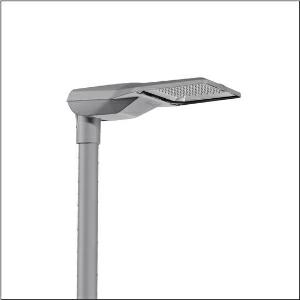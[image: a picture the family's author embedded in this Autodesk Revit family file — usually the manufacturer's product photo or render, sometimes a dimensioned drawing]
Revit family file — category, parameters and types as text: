
# Revit family: streetlight_sl_21_iq_midi___stw1_0a_5xe3e41g08mb_cdbd
name_source: partatom
category: Lighting Fixtures
units: mm (PartAtom-declared; Revit-internal decimal feet)

## family parameters
Cut with Voids When Loaded = No
Host = Face
Light Source = No
Part Type = Normal
Room Calculation Point = No
Round Connector Dimension = Use Diameter
Shared = No

## types (1)
- --- (1 x LED, 20360 lm, 146.7 W, 4000K)
    Apparent Load = 147 VA
    CIE Flux Codes = 38 75 98 100 100
    Color Rendering = 70
    Color Temperature = 4000K
    Default Elevation = 1800 mm
    Description = Streetlight SL 21 iQ midi, mast luminaire, primary light control with lens, of PMMA, primary optical cover: cover, of toughened safety glass, transparent, light distribution: STW1.0a, light emission: direct distribution, primary light characteristic: asymmetric, installation type: post-top, side-entry, LED, High Power LED, rated luminous flux: 20.360lm, luminous efficacy: 139lm/W, light colour: 740, colour temperature: 4000K, control: Street-Remote, Auto-Match, Temp-Guard, Lumen-Switch, Night-Set, Smart-Wire, Light-Fading, Desk-Remote (wireless, voltage-free reading and setting of iQ features in the workshop via application-optimized NFC function/RFID function), optimised constant luminous flux control (CLO 2.0), presetting dimming linear, mains connection: 230..240V, AC, 50/60Hz, start of lifetime: 147W, end of service life: 161W, reduction: 62W, luminaire housing, of diecast aluminium, powder-coated, Siteco® metallic grey (DB 702S), corrosivity category C5 mid according to DIN EN ISO 12944, please order mast flange separately, inclination adjustable: 0°, 5°, 10°, 15°, sealing non-destructively replaceable, multi-level sealing system, length: 644mm, width: 335mm, height: 110mm, mast flange for spigot size: 42mm (side-entry): 5XC10008XM4, 60/48mm (side-entry/post-top): 5XC10108XM2, 76/60mm (side-entry/post-top): 5XC10108XM1, protection rating (complete): IP66, insulation class (complete): insulation class II (safety insulation), certification: CE, ENEC, ENEC+, VDE, impact resistance: IK09, permissible operating ambient temperature for outdoor applications: -40..+50°C, standard-compliant lighting for roads and squares, packaging unit: 1 piece

Light Distribution: STW1.0a
    Height = 111 mm
    Lamp = 1 x LED
    Lamp Light Flux = 20360 lm
    Lamp Power = 146.7 W
    Lamp count = 1
    Length = 644 mm
    Luminous efficacy = 139 lm/W
    Manufacturer = Siteco
    ModVariant = No
    Model = 5XE3E41G08MB
    Number of Poles = 1
    OnlyDefault = Yes
    Power Factor = 1
    Product Name = Streetlight SL 21 iQ midi | STW1.0a
    Product group = mast luminaire | pylon top
    ProductGroupID = 6100
    Protection Class = Protection class II
    Protection Degree = IP 66
    RLX_Detail_Level = 1
    RLX_Emergency_Light_Flux = 0 lm
    RLX_Emergency_Type = 0
    RLX_Emergency_Type_DB = No
    RlxData = <blob elided: 90533 chars, md5=682005c8>
    Socket = socket
    Standby Power = 0 W
    System Light Flux = 20360 lm
    System Power = 147 W
    Type Comments = factory setting: luminous flux: 100 % | dim-lin: 254 | 753 mA
    Type Image = l_1004298.jpg
    URL = http://relux.com
    VarID = @adj_140081
    Voltage = 0 V
    Weight = 0.00 kg
    Width = 336 mm

## geometry (parser evidence)
native form markers: Blend x4, Sweep x10
no freeform markers — native parametric forms only
